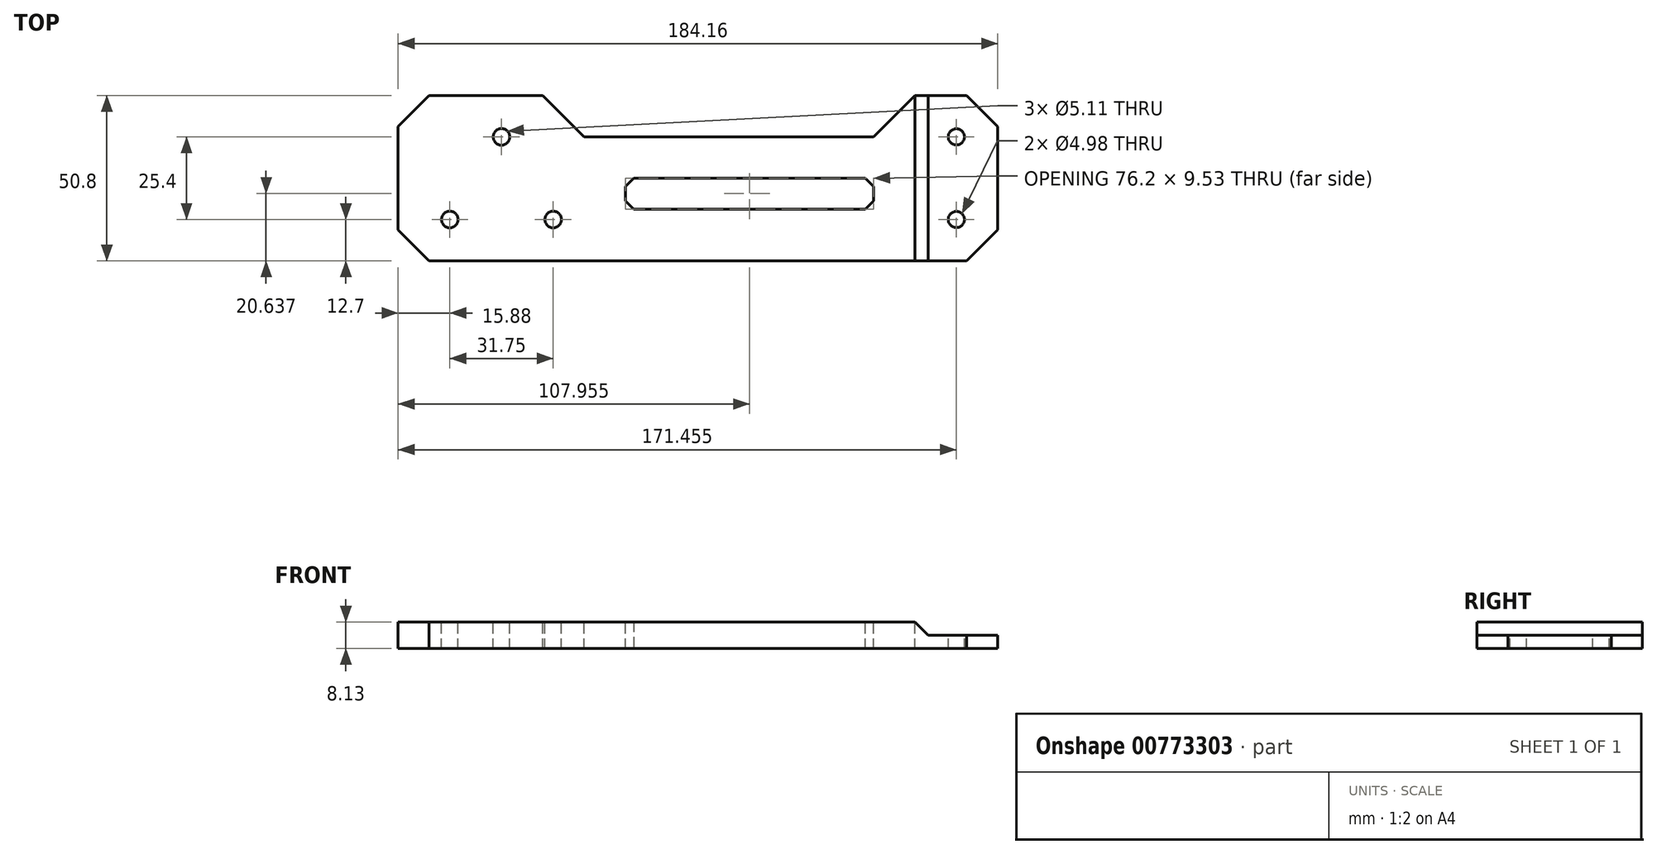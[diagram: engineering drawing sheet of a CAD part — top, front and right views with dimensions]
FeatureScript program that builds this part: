
annotation { "Feature Type Name" : "Feature", "Feature Type Description" : "" }
export const myFeature = defineFeature(function(context is Context, id is Id, definition is map)
    precondition{}
    {
        {
            var Q0;
            Q0=qCreatedBy(makeId("Top.planeOp"),FACE);
            var sketch = newSketch(context, id + "F0", { "sketchPlane" : qUnion([Q0])});
            skLineSegment(sketch, "E0.bottom", {"start": v(-92.08, 25.4) * mm, "end": v(92.08, 25.4) * mm});
            skLineSegment(sketch, "E0.top", {"start": v(-92.08, -25.4) * mm, "end": v(92.08, -25.4) * mm});
            skLineSegment(sketch, "E0.left", {"start": v(-92.08, 25.4) * mm, "end": v(-92.08, -25.4) * mm});
            skLineSegment(sketch, "E0.right", {"start": v(92.08, 25.4) * mm, "end": v(92.08, -25.4) * mm});
            skPoint(sketch, "E0.middle", {"position": v(0, 0) * mm});
            skSolve(sketch);
        }
        {
            var Q0;
            Q0=makeQuery(id+"F0.imprint","IMPRINT",FACE,{"disambiguationData":[TD([[makeQuery(id+"F0.imprint","IMPRINT",EDGE,{"derivedFrom":sQuery(id+"F0.wireOp",EDGE,"E0.bottom")}),-1.0]])]});
            extrude(context, id + "F1", {"entities" : qUnion([Q0]), "depth" : 8.13 * mm, "offsetDistance" : 25.4 * mm});
        }
        {
            var Q0;
            Q0=makeQuery(id+"F1.opExtrude","CAP_FACE",FACE,{"disambiguationData":[OSD([sQuery(id+"F0.wireOp",EDGE,"E0.bottom"),sQuery(id+"F0.wireOp",EDGE,"E0.top"),sQuery(id+"F0.wireOp",EDGE,"E0.left"),sQuery(id+"F0.wireOp",EDGE,"E0.right")])],"isStart":false});
            var sketch = newSketch(context, id + "F2", { "sketchPlane" : qUnion([Q0])});
            skPoint(sketch, "E1", {"position": v(-76.2, -12.7) * mm});
            skPoint(sketch, "E2", {"position": v(-44.45, -12.7) * mm});
            skPoint(sketch, "E3", {"position": v(-60.33, 12.7) * mm});
            skSolve(sketch);
        }
        {
            var Q0;
            Q0=sQuery(id+"F2.wireOp",VERTEX,"E3");
            var Q1;
            Q1=sQuery(id+"F2.wireOp",VERTEX,"E1");
            var Q2;
            Q2=sQuery(id+"F2.wireOp",VERTEX,"E2");
            var Q3;
            Q3=makeQuery(id+"F1.opExtrude","SWEPT_BODY",BODY,{"disambiguationData":[OSD([sQuery(id+"F0.wireOp",EDGE,"E0.bottom"),sQuery(id+"F0.wireOp",EDGE,"E0.top"),sQuery(id+"F0.wireOp",EDGE,"E0.left"),sQuery(id+"F0.wireOp",EDGE,"E0.right")])]});
            hole(context, id + "F3", {"style" : HoleStyle.SIMPLE, "endStyle" : HoleEndStyle.THROUGH, "standardTappedOrClearance" : lookupTablePath({ "standard" : "ANSI", "fit" : "Normal (ASME)", "size" : "#10", "type" : "Clearance" }), "standardBlindInLast" : lookupTablePath({ "fit" : "Free", "standard" : "ANSI", "size" : "#10", "type" : "Clearance" }), "holeDiameter" : 5.1 * mm, "majorDiameter" : 6.35 * mm, "isTappedThrough" : true, "tappedDepth" : 12.7 * mm, "tapClearance" : 3, "locations" : qUnion([Q0, Q1, Q2]), "scope" : qUnion([Q3])});
        }
        {
            var Q0;
            Q0=qCreatedBy(makeId("Right.planeOp"),FACE);
            cPlane(context, id + "F4", {"entities" : qUnion([Q0]), "cplaneType" : CPlaneType.OFFSET, "offset" : 60.32 * mm, "oppositeDirection" : true, "width" : 152.4 * mm, "height" : 152.4 * mm});
        }
        {
            var Q0;
            Q0=makeQuery(id+"F1.opExtrude","CAP_FACE",FACE,{"disambiguationData":[OSD([sQuery(id+"F0.wireOp",EDGE,"E0.bottom"),sQuery(id+"F0.wireOp",EDGE,"E0.top"),sQuery(id+"F0.wireOp",EDGE,"E0.left"),sQuery(id+"F0.wireOp",EDGE,"E0.right")])],"isStart":false});
            var sketch = newSketch(context, id + "F5", { "sketchPlane" : qUnion([Q0])});
            skPoint(sketch, "E4", {"position": v(79.38, 12.7) * mm});
            skPoint(sketch, "E5", {"position": v(79.38, -12.7) * mm});
            skSolve(sketch);
        }
        {
            var Q0;
            Q0=sQuery(id+"F5.wireOp",VERTEX,"E4");
            var Q1;
            Q1=sQuery(id+"F5.wireOp",VERTEX,"E5");
            var Q2;
            Q2=makeQuery(id+"F1.opExtrude","SWEPT_BODY",BODY,{"disambiguationData":[OSD([sQuery(id+"F0.wireOp",EDGE,"E0.bottom"),sQuery(id+"F0.wireOp",EDGE,"E0.top"),sQuery(id+"F0.wireOp",EDGE,"E0.left"),sQuery(id+"F0.wireOp",EDGE,"E0.right")])]});
            hole(context, id + "F6", {"style" : HoleStyle.SIMPLE, "endStyle" : HoleEndStyle.THROUGH, "standardTappedOrClearance" : lookupTablePath({ "standard" : "ANSI", "fit" : "Close", "size" : "#10", "type" : "Clearance" }), "standardBlindInLast" : lookupTablePath({ "fit" : "Close", "standard" : "ANSI", "size" : "#10", "type" : "Clearance" }), "holeDiameter" : 4.98 * mm, "majorDiameter" : 6.35 * mm, "isTappedThrough" : true, "tappedDepth" : 12.7 * mm, "tapClearance" : 3, "locations" : qUnion([Q0, Q1]), "scope" : qUnion([Q2])});
        }
        {
            var Q0;
            Q0=makeQuery(id+"F1.opExtrude","CAP_FACE",FACE,{"disambiguationData":[OSD([sQuery(id+"F0.wireOp",EDGE,"E0.bottom"),sQuery(id+"F0.wireOp",EDGE,"E0.top"),sQuery(id+"F0.wireOp",EDGE,"E0.left"),sQuery(id+"F0.wireOp",EDGE,"E0.right")])],"isStart":false});
            var sketch = newSketch(context, id + "F7", { "sketchPlane" : qUnion([Q0])});
            skLineSegment(sketch, "E6", {"start": v(-47.63, 25.4) * mm, "end": v(-34.92, 12.7) * mm});
            skLineSegment(sketch, "E7", {"start": v(-34.92, 12.7) * mm, "end": v(53.98, 12.7) * mm});
            skLineSegment(sketch, "E8", {"start": v(53.98, 12.7) * mm, "end": v(66.67, 25.4) * mm});
            skLineSegment(sketch, "E9", {"start": v(66.67, 25.4) * mm, "end": v(-47.63, 25.4) * mm});
            skLineSegment(sketch, "E10.bottom", {"start": v(-22.23, 0) * mm, "end": v(53.98, 0) * mm});
            skLineSegment(sketch, "E10.top", {"start": v(-22.23, -9.53) * mm, "end": v(53.98, -9.53) * mm});
            skLineSegment(sketch, "E10.left", {"start": v(-22.23, 0) * mm, "end": v(-22.23, -9.53) * mm});
            skLineSegment(sketch, "E10.right", {"start": v(53.98, 0) * mm, "end": v(53.98, -9.53) * mm});
            skPoint(sketch, "E10.middle", {"position": v(15.88, -4.76) * mm});
            skSolve(sketch);
        }
        {
            var Q0;
            Q0=makeQuery(id+"F7.imprint","IMPRINT",FACE,{"disambiguationData":[TD([[makeQuery(id+"F7.imprint","IMPRINT",EDGE,{"derivedFrom":sQuery(id+"F7.wireOp",EDGE,"E6")}),1.0]])]});
            var Q1;
            Q1=makeQuery(id+"F7.imprint","IMPRINT",FACE,{"disambiguationData":[TD([[makeQuery(id+"F7.imprint","IMPRINT",EDGE,{"derivedFrom":sQuery(id+"F7.wireOp",EDGE,"E10.bottom")}),-1.0]])]});
            extrude(context, id + "F8", {"entities" : qUnion([Q0, Q1]), "operationType" : NewBodyOperationType.REMOVE, "endBound" : BoundingType.THROUGH_ALL, "oppositeDirection" : true, "depth" : 25.4 * mm, "offsetDistance" : 25.4 * mm});
        }
        {
            var Q0;
            Q0=makeQuery(id+"F1.opExtrude","SWEPT_EDGE",EDGE,{"disambiguationData":[OSD([sQuery(id+"F0.wireOp",EDGE,"E0.top"),sQuery(id+"F0.wireOp",EDGE,"E0.left")])]});
            var Q1;
            Q1=makeQuery(id+"F1.opExtrude","SWEPT_EDGE",EDGE,{"disambiguationData":[OSD([sQuery(id+"F0.wireOp",EDGE,"E0.bottom"),sQuery(id+"F0.wireOp",EDGE,"E0.left")])]});
            var Q2;
            Q2=makeQuery(id+"F1.opExtrude","SWEPT_EDGE",EDGE,{"disambiguationData":[OSD([sQuery(id+"F0.wireOp",EDGE,"E0.top"),sQuery(id+"F0.wireOp",EDGE,"E0.right")])]});
            var Q3;
            Q3=makeQuery(id+"F1.opExtrude","SWEPT_EDGE",EDGE,{"disambiguationData":[OSD([sQuery(id+"F0.wireOp",EDGE,"E0.bottom"),sQuery(id+"F0.wireOp",EDGE,"E0.right")])]});
            chamfer(context, id + "F9", {"entities" : qUnion([Q0, Q1, Q2, Q3]), "width" : 9.52 * mm, "tangentPropagation" : true});
        }
        {
            var Q0;
            Q0=makeQuery(id+"F8.boolean.opBoolean","COPY",EDGE,{"derivedFrom":makeQuery(id+"F8.opExtrude","SWEPT_EDGE",EDGE,{"disambiguationData":[OSD([sQuery(id+"F7.wireOp",EDGE,"E10.bottom"),sQuery(id+"F7.wireOp",EDGE,"E10.left")])]})});
            var Q1;
            Q1=makeQuery(id+"F8.boolean.opBoolean","COPY",EDGE,{"derivedFrom":makeQuery(id+"F8.opExtrude","SWEPT_EDGE",EDGE,{"disambiguationData":[OSD([sQuery(id+"F7.wireOp",EDGE,"E10.top"),sQuery(id+"F7.wireOp",EDGE,"E10.left")])]})});
            var Q2;
            Q2=makeQuery(id+"F8.boolean.opBoolean","COPY",EDGE,{"derivedFrom":makeQuery(id+"F8.opExtrude","SWEPT_EDGE",EDGE,{"disambiguationData":[OSD([sQuery(id+"F7.wireOp",EDGE,"E10.bottom"),sQuery(id+"F7.wireOp",EDGE,"E10.right")])]})});
            var Q3;
            Q3=makeQuery(id+"F8.boolean.opBoolean","COPY",EDGE,{"derivedFrom":makeQuery(id+"F8.opExtrude","SWEPT_EDGE",EDGE,{"disambiguationData":[OSD([sQuery(id+"F7.wireOp",EDGE,"E10.top"),sQuery(id+"F7.wireOp",EDGE,"E10.right")])]})});
            chamfer(context, id + "F10", {"entities" : qUnion([Q0, Q1, Q2, Q3]), "width" : 2.54 * mm, "tangentPropagation" : true});
        }
        {
            var Q0;
            Q0=makeQuery(id+"F1.opExtrude","CAP_FACE",FACE,{"disambiguationData":[OSD([sQuery(id+"F0.wireOp",EDGE,"E0.bottom"),sQuery(id+"F0.wireOp",EDGE,"E0.top"),sQuery(id+"F0.wireOp",EDGE,"E0.left"),sQuery(id+"F0.wireOp",EDGE,"E0.right")])],"isStart":false});
            var sketch = newSketch(context, id + "F11", { "sketchPlane" : qUnion([Q0])});
            skLineSegment(sketch, "E11", {"start": v(66.67, 25.4) * mm, "end": v(66.67, -25.4) * mm});
            skLineSegment(sketch, "E12", {"start": v(66.67, -25.4) * mm, "end": v(82.55, -25.4) * mm});
            skLineSegment(sketch, "E13", {"start": v(82.55, -25.4) * mm, "end": v(92.08, -15.88) * mm});
            skLineSegment(sketch, "E14", {"start": v(92.08, -15.88) * mm, "end": v(92.08, 15.88) * mm});
            skLineSegment(sketch, "E15", {"start": v(92.08, 15.88) * mm, "end": v(82.55, 25.4) * mm});
            skLineSegment(sketch, "E16", {"start": v(82.55, 25.4) * mm, "end": v(66.67, 25.4) * mm});
            skSolve(sketch);
        }
        {
            var Q0;
            Q0=makeQuery(id+"F11.imprint","IMPRINT",FACE,{"disambiguationData":[TD([[makeQuery(id+"F11.imprint","IMPRINT",EDGE,{"derivedFrom":sQuery(id+"F11.wireOp",EDGE,"E11")}),1.0]])]});
            extrude(context, id + "F12", {"entities" : qUnion([Q0]), "operationType" : NewBodyOperationType.REMOVE, "oppositeDirection" : true, "depth" : 4.06 * mm, "offsetDistance" : 25.4 * mm});
        }
        {
            var Q0;
            Q0=makeQuery(id+"F12.boolean.opBoolean","COPY",EDGE,{"derivedFrom":makeQuery(id+"F12.opExtrude","CAP_EDGE",EDGE,{"disambiguationData":[OSD([sQuery(id+"F11.wireOp",EDGE,"E11")])],"isStart":false})});
            chamfer(context, id + "F13", {"entities" : qUnion([Q0]), "width" : 4.06 * mm, "tangentPropagation" : true});
        }
        {
            var Q0;
            Q0=makeQuery(id+"F1.opExtrude","SWEPT_FACE",FACE,{"disambiguationData":[OSD([sQuery(id+"F0.wireOp",EDGE,"E0.right")])]});
            cPlane(context, id + "F14", {"entities" : qUnion([Q0]), "cplaneType" : CPlaneType.OFFSET, "offset" : 0 * mm, "width" : 152.4 * mm, "height" : 152.4 * mm});
        }
    });
